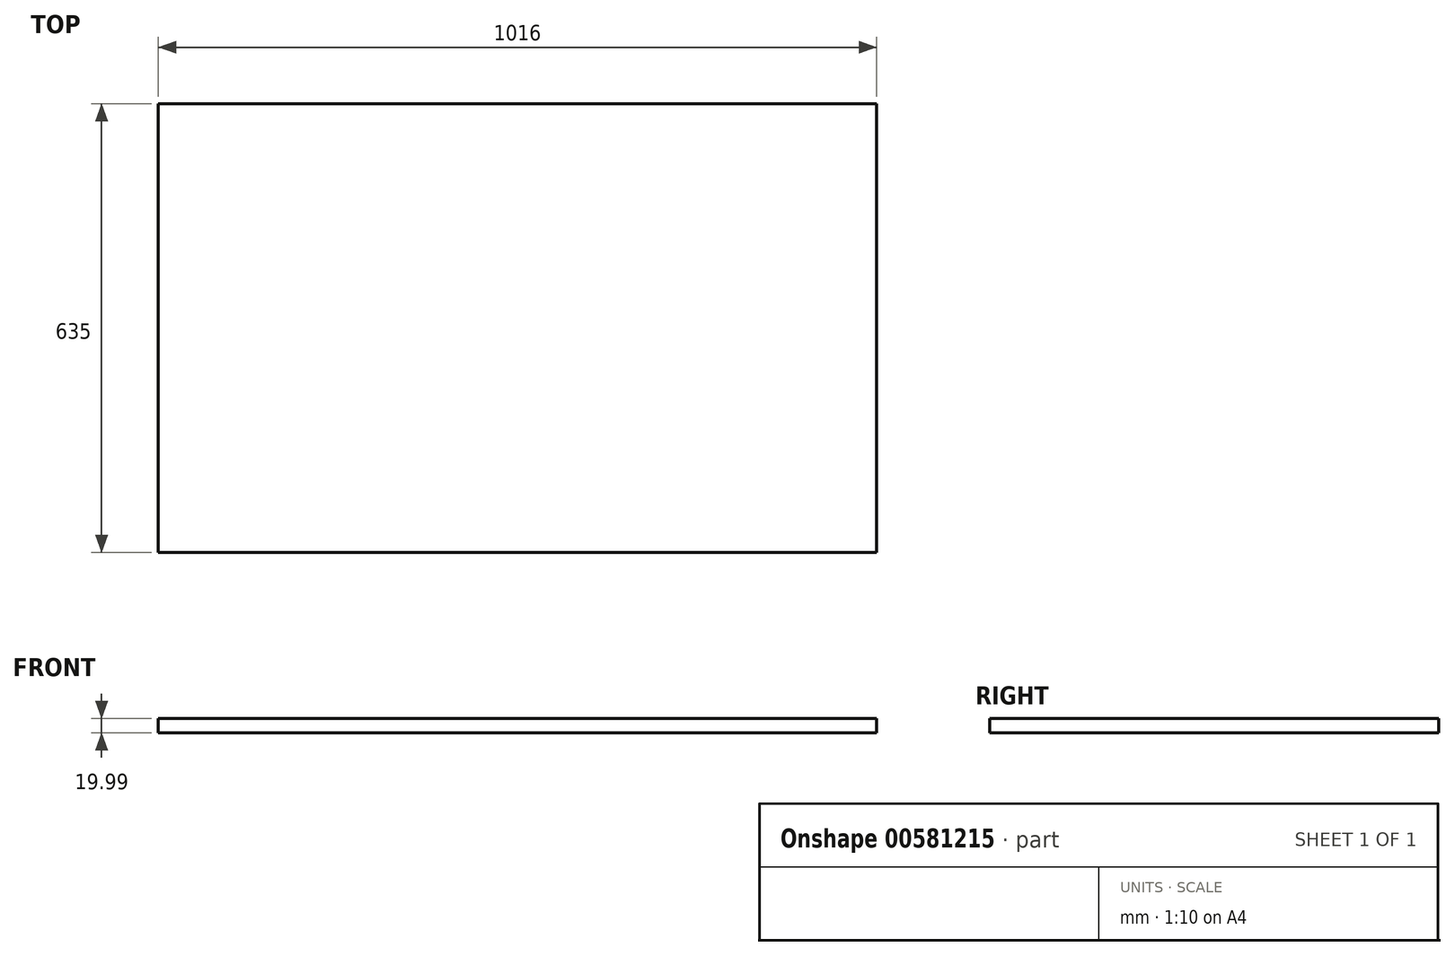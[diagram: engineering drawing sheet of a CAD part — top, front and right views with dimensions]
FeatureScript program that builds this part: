
annotation { "Feature Type Name" : "Feature", "Feature Type Description" : "" }
export const myFeature = defineFeature(function(context is Context, id is Id, definition is map)
    precondition{}
    {
        {
            var Q0;
            Q0=qCreatedBy(makeId("Top.planeOp"),FACE);
            var sketch = newSketch(context, id + "F0", { "sketchPlane" : qUnion([Q0])});
            skLineSegment(sketch, "E0.bottom", {"start": v(484.3, 368.56) * mm, "end": v(-531.7, 368.56) * mm});
            skLineSegment(sketch, "E0.top", {"start": v(484.3, -266.44) * mm, "end": v(-531.7, -266.44) * mm});
            skLineSegment(sketch, "E0.left", {"start": v(484.3, 368.56) * mm, "end": v(484.3, -266.44) * mm});
            skLineSegment(sketch, "E0.right", {"start": v(-531.7, 368.56) * mm, "end": v(-531.7, -266.44) * mm});
            skPoint(sketch, "E0.middle", {"position": v(-23.7, 51.06) * mm});
            skSolve(sketch);
        }
        {
            var Q0;
            Q0 = qSketchRegion(id + "F0", true);
            extrude(context, id + "F1", {"entities" : qUnion([Q0]), "depth" : 19.99 * mm, "offsetDistance" : 25.4 * mm});
        }
    });
